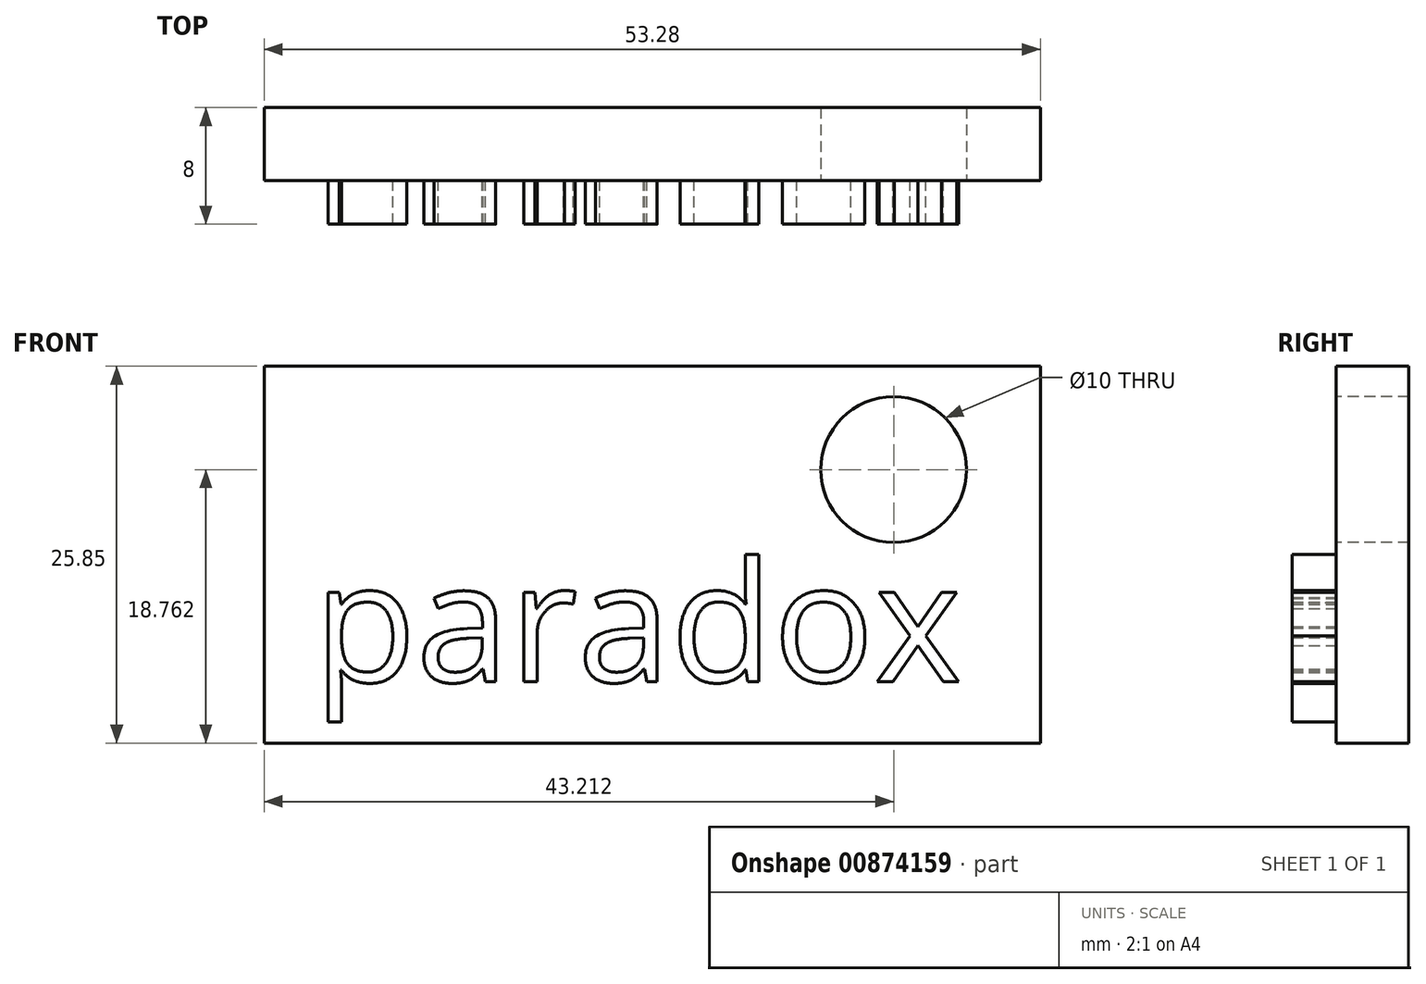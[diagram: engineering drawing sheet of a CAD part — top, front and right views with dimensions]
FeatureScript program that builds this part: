
annotation { "Feature Type Name" : "Feature", "Feature Type Description" : "" }
export const myFeature = defineFeature(function(context is Context, id is Id, definition is map)
    precondition{}
    {
        {
            var Q0;
            Q0=qCreatedBy(makeId("Front.planeOp"),FACE);
            var sketch = newSketch(context, id + "F0", { "sketchPlane" : qUnion([Q0])});
            skLineSegment(sketch, "E0.bottom", {"start": v(0, 0) * mm, "end": v(53.28, 0) * mm});
            skLineSegment(sketch, "E0.top", {"start": v(0, 25.85) * mm, "end": v(53.28, 25.85) * mm});
            skLineSegment(sketch, "E0.left", {"start": v(0, 0) * mm, "end": v(0, 25.85) * mm});
            skLineSegment(sketch, "E0.right", {"start": v(53.28, 0) * mm, "end": v(53.28, 25.85) * mm});
            skSolve(sketch);
        }
        {
            var Q0;
            Q0 = qSketchRegion(id + "F0", true);
            extrude(context, id + "F1", {"entities" : qUnion([Q0]), "depth" : 5 * mm, "offsetDistance" : 25 * mm});
        }
        {
            var Q0;
            Q0=makeQuery(id+"F1.opExtrude","CAP_FACE",FACE,{"disambiguationData":[OSD([sQuery(id+"F0.wireOp",EDGE,"E0.bottom"),sQuery(id+"F0.wireOp",EDGE,"E0.top"),sQuery(id+"F0.wireOp",EDGE,"E0.left"),sQuery(id+"F0.wireOp",EDGE,"E0.right")])],"isStart":false});
            var sketch = newSketch(context, id + "F2", { "sketchPlane" : qUnion([Q0])});
            skText(sketch, "E1", { "text": "paradox", "fontName": "OpenSans-Regular.ttf"});
            const initialGuessF2  = {"E1": [0.0034, 0.0042, 1, 0, 0.00827]};
            skSetInitialGuess(sketch, initialGuessF2);
            skSolve(sketch);
        }
        {
            var Q0;
            Q0 = qSketchRegion(id + "F2", true);
            extrude(context, id + "F3", {"entities" : qUnion([Q0]), "operationType" : NewBodyOperationType.ADD, "depth" : 3 * mm, "offsetDistance" : 25 * mm});
        }
        {
            var Q0;
            {var subQ0=sQuery(id+"F0.wireOp",EDGE,"E0.top");var subQ1=sQuery(id+"F0.wireOp",EDGE,"E0.right");var subQ2=sQuery(id+"F0.wireOp",EDGE,"E0.bottom");var subQ3=sQuery(id+"F0.wireOp",EDGE,"E0.left");Q0=makeQuery(id+"F3.boolean.opBoolean","SPLIT",FACE,{"disambiguationData":[TD([makeQuery(id+"F1.opExtrude","SWEPT_FACE",FACE,{"disambiguationData":[OSD([subQ2])]})])],"derivedFrom":makeQuery(id+"F1.opExtrude","CAP_FACE",FACE,{"disambiguationData":[OSD([subQ2,subQ0,subQ3,subQ1])],"isStart":false})});}
            var sketch = newSketch(context, id + "F4", { "sketchPlane" : qUnion([Q0])});
            skCircle(sketch, "E2", {"center": v(43.21, 18.76) * mm, "radius": 5 * mm});
            skSolve(sketch);
        }
        {
            var Q0;
            Q0=makeQuery(id+"F4.imprint","IMPRINT",FACE,{"disambiguationData":[TD([[makeQuery(id+"F4.imprint","IMPRINT",EDGE,{"derivedFrom":sQuery(id+"F4.wireOp",EDGE,"E2")}),1.0]])]});
            extrude(context, id + "F5", {"entities" : qUnion([Q0]), "operationType" : NewBodyOperationType.REMOVE, "oppositeDirection" : true, "depth" : 5 * mm, "offsetDistance" : 25 * mm});
        }
    });
